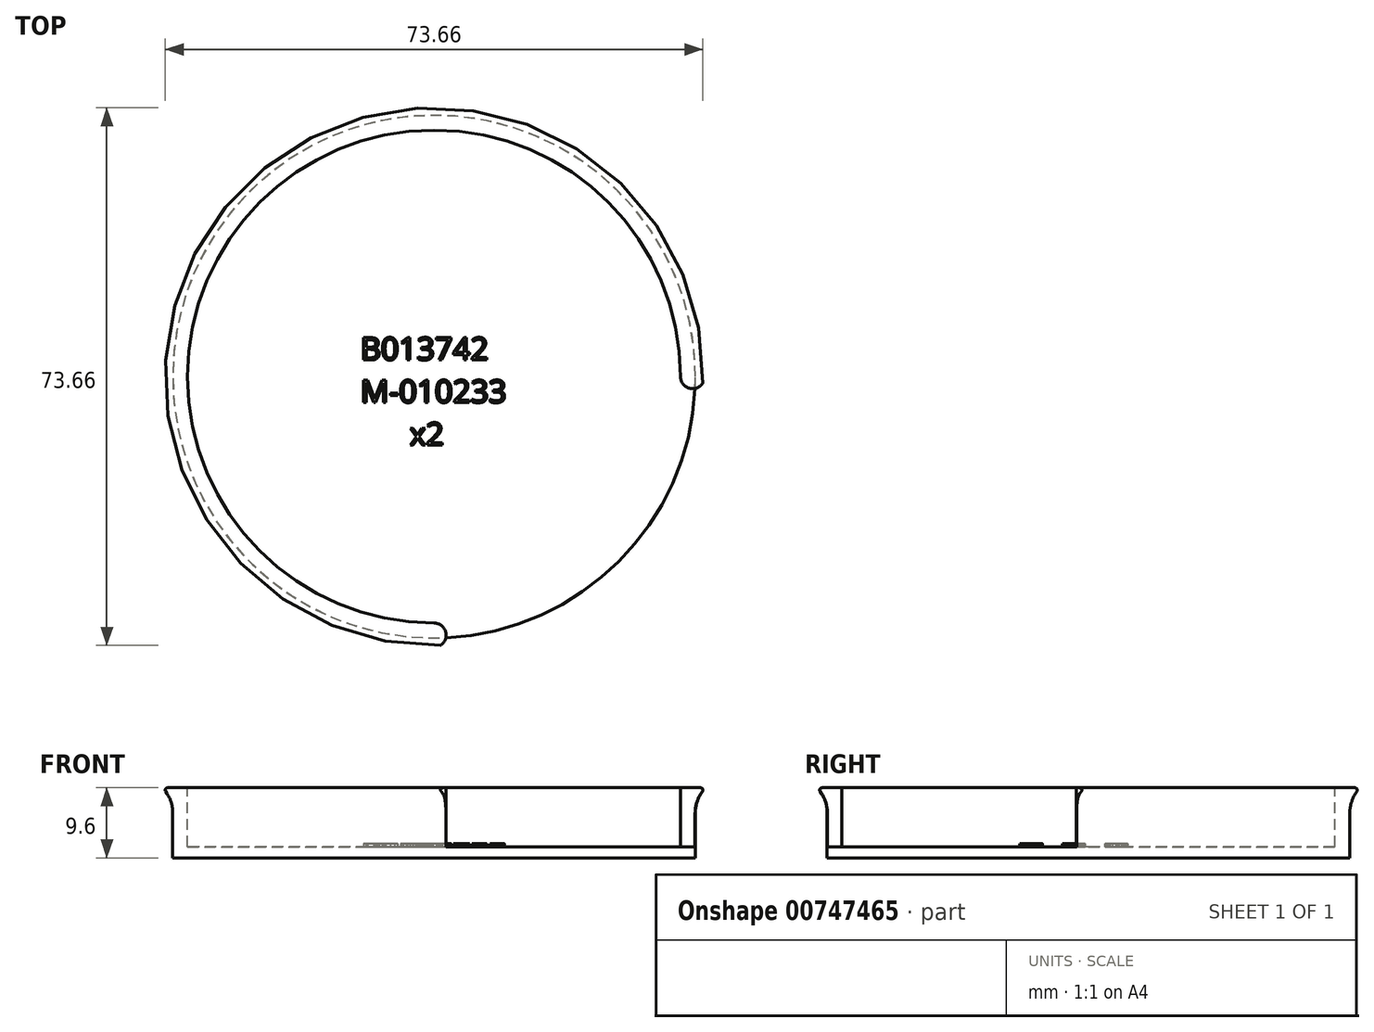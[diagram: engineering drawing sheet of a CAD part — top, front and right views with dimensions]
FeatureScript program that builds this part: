
annotation { "Feature Type Name" : "Feature", "Feature Type Description" : "" }
export const myFeature = defineFeature(function(context is Context, id is Id, definition is map)
    precondition{}
    {
        {
            var Q0;
            Q0=qCreatedBy(makeId("Right.planeOp"),FACE);
            var sketch = newSketch(context, id + "F0", { "sketchPlane" : qUnion([Q0])});
            skLineSegment(sketch, "E0", {"start": v(-27.34, 9.6) * mm, "end": v(-27.34, 0) * mm});
            skLineSegment(sketch, "E1", {"start": v(-27.34, 9.6) * mm, "end": v(-64.4, 9.6) * mm});
            skLineSegment(sketch, "E2", {"start": v(-27.34, 0) * mm, "end": v(-63.14, 0) * mm});
            skLineSegment(sketch, "E3", {"start": v(-63.14, 0) * mm, "end": v(-63.14, 7.57) * mm});
            skLineSegment(sketch, "E4", {"start": v(-63.14, 7.57) * mm, "end": v(-63.14, 9.6) * mm});
            skLineSegment(sketch, "E5", {"start": v(-64.4, 9.6) * mm, "end": v(-63.14, 7.57) * mm});
            skSolve(sketch);
        }
        {
            var Q0;
            Q0=qSketchRegion(id+"F0",true);
            var Q1;
            Q1=sQuery(id+"F0.wireOp",EDGE,"E0");
            revolve(context, id + "F1", {"entities" : qUnion([Q0]), "axis" : qUnion([Q1]), "revolveType" : RevolveType.FULL});
        }
        {
            var Q0;
            Q0=makeQuery(id+"F1.opRevolve","SWEPT_FACE",FACE,{"disambiguationData":[OSD([sQuery(id+"F0.wireOp",EDGE,"E1")])]});
            var sketch = newSketch(context, id + "F2", { "sketchPlane" : qUnion([Q0])});
            skCircle(sketch, "E6", {"center": v(0, -27.34) * mm, "radius": 33.77 * mm});
            skLineSegment(sketch, "E7.bottom", {"start": v(0, -27.34) * mm, "end": v(37.07, -27.34) * mm});
            skLineSegment(sketch, "E7.top", {"start": v(0, -64.4) * mm, "end": v(37.07, -64.4) * mm});
            skLineSegment(sketch, "E7.left", {"start": v(0, -27.34) * mm, "end": v(0, -64.4) * mm});
            skLineSegment(sketch, "E7.right", {"start": v(37.07, -27.34) * mm, "end": v(37.07, -64.4) * mm});
            skArc(sketch, "E8", {"start": v(0, -64.4) * mm, "mid": v(1.65, -62.76) * mm, "end": v(0, -61.1) * mm});
            skArc(sketch, "E9", {"start": v(33.77, -27.34) * mm, "mid": v(35.42, -28.99) * mm, "end": v(37.07, -27.34) * mm});
            skSolve(sketch);
        }
        {
            var Q0;
            {var subQ0=sQuery(id+"F2.wireOp",EDGE,"E7.left");var subQ3=sQuery(id+"F2.wireOp",EDGE,"E7.bottom");var subQ5=makeQuery(id+"F2.imprint","INTERSECT",VERTEX,{"derivedFrom":[subQ3,subQ0]});Q0=makeQuery(id+"F2.imprint","IMPRINT",FACE,{"disambiguationData":[TD([[makeQuery(id+"F2.imprint","IMPRINT",EDGE,{"disambiguationData":[TD([[subQ5,-1.0]])],"derivedFrom":subQ3}),1.0]])]});}
            var Q1;
            {var subQ0=sQuery(id+"F2.wireOp",EDGE,"E7.left");var subQ3=sQuery(id+"F2.wireOp",EDGE,"E7.bottom");var subQ5=makeQuery(id+"F2.imprint","INTERSECT",VERTEX,{"derivedFrom":[subQ3,subQ0]});Q1=makeQuery(id+"F2.imprint","IMPRINT",FACE,{"disambiguationData":[TD([[makeQuery(id+"F2.imprint","IMPRINT",EDGE,{"disambiguationData":[TD([[subQ5,-1.0]])],"derivedFrom":subQ3}),-1.0]])]});}
            var Q2;
            {var subQ0=sQuery(id+"F2.wireOp",EDGE,"E8");Q2=makeQuery(id+"F2.imprint","IMPRINT",FACE,{"disambiguationData":[TD([[makeQuery(id+"F2.imprint","IMPRINT",EDGE,{"derivedFrom":subQ0}),-1.0]])]});}
            extrude(context, id + "F3", {"entities" : qUnion([Q0, Q1, Q2]), "operationType" : NewBodyOperationType.REMOVE, "oppositeDirection" : true, "depth" : 8.08 * mm});
        }
        {
            var Q0;
            Q0=makeQuery(id+"F1.opRevolve","SWEPT_EDGE",EDGE,{"disambiguationData":[OSD([sQuery(id+"F0.wireOp",EDGE,"E1"),sQuery(id+"F0.wireOp",EDGE,"E5")])]});
            var Q1;
            Q1=makeQuery(id+"F3.boolean.opBoolean","COPY",EDGE,{"derivedFrom":makeQuery(id+"F3.opExtrude","CAP_EDGE",EDGE,{"disambiguationData":[OSD([sQuery(id+"F2.wireOp",EDGE,"E6")])],"isStart":true})});
            fillet(context, id + "F4", {"entities" : qUnion([Q0, Q1]), "radius" : 0.3 * mm, "tangentPropagation" : true, "allowEdgeOverflow" : false});
        }
        {
            var Q0;
            Q0=makeQuery(id+"F1.opRevolve","SWEPT_EDGE",EDGE,{"disambiguationData":[OSD([sQuery(id+"F0.wireOp",EDGE,"E3"),sQuery(id+"F0.wireOp",EDGE,"E4"),sQuery(id+"F0.wireOp",EDGE,"E5")])]});
            fillet(context, id + "F5", {"entities" : qUnion([Q0]), "radius" : 5 * mm, "tangentPropagation" : true, "allowEdgeOverflow" : false});
        }
        {
            var Q0;
            Q0=makeQuery(id+"F3.boolean.opBoolean","COPY",FACE,{"derivedFrom":makeQuery(id+"F3.opExtrude","CAP_FACE",FACE,{"disambiguationData":[OSD([sQuery(id+"F0.wireOp",EDGE,"E1"),sQuery(id+"F0.wireOp",EDGE,"E5"),sQuery(id+"F2.wireOp",EDGE,"E6"),sQuery(id+"F2.wireOp",EDGE,"E8"),sQuery(id+"F2.wireOp",EDGE,"E9")])],"isStart":false})});
            var sketch = newSketch(context, id + "F6", { "sketchPlane" : qUnion([Q0])});
            skText(sketch, "E10", { "text": "B013742\nM-010233\n      x2", "fontName": "OpenSans-Regular.ttf"});
            const initialGuessF6  = {"E10": [-0.01006, -0.02505, 1, 0, 0.00309]};
            skSetInitialGuess(sketch, initialGuessF6);
            skSolve(sketch);
        }
        {
            var Q0;
            Q0=qSketchRegion(id+"F6",true);
            extrude(context, id + "F7", {"entities" : qUnion([Q0]), "operationType" : NewBodyOperationType.ADD, "depth" : 0.4 * mm, "offsetDistance" : 25 * mm});
        }
    });
